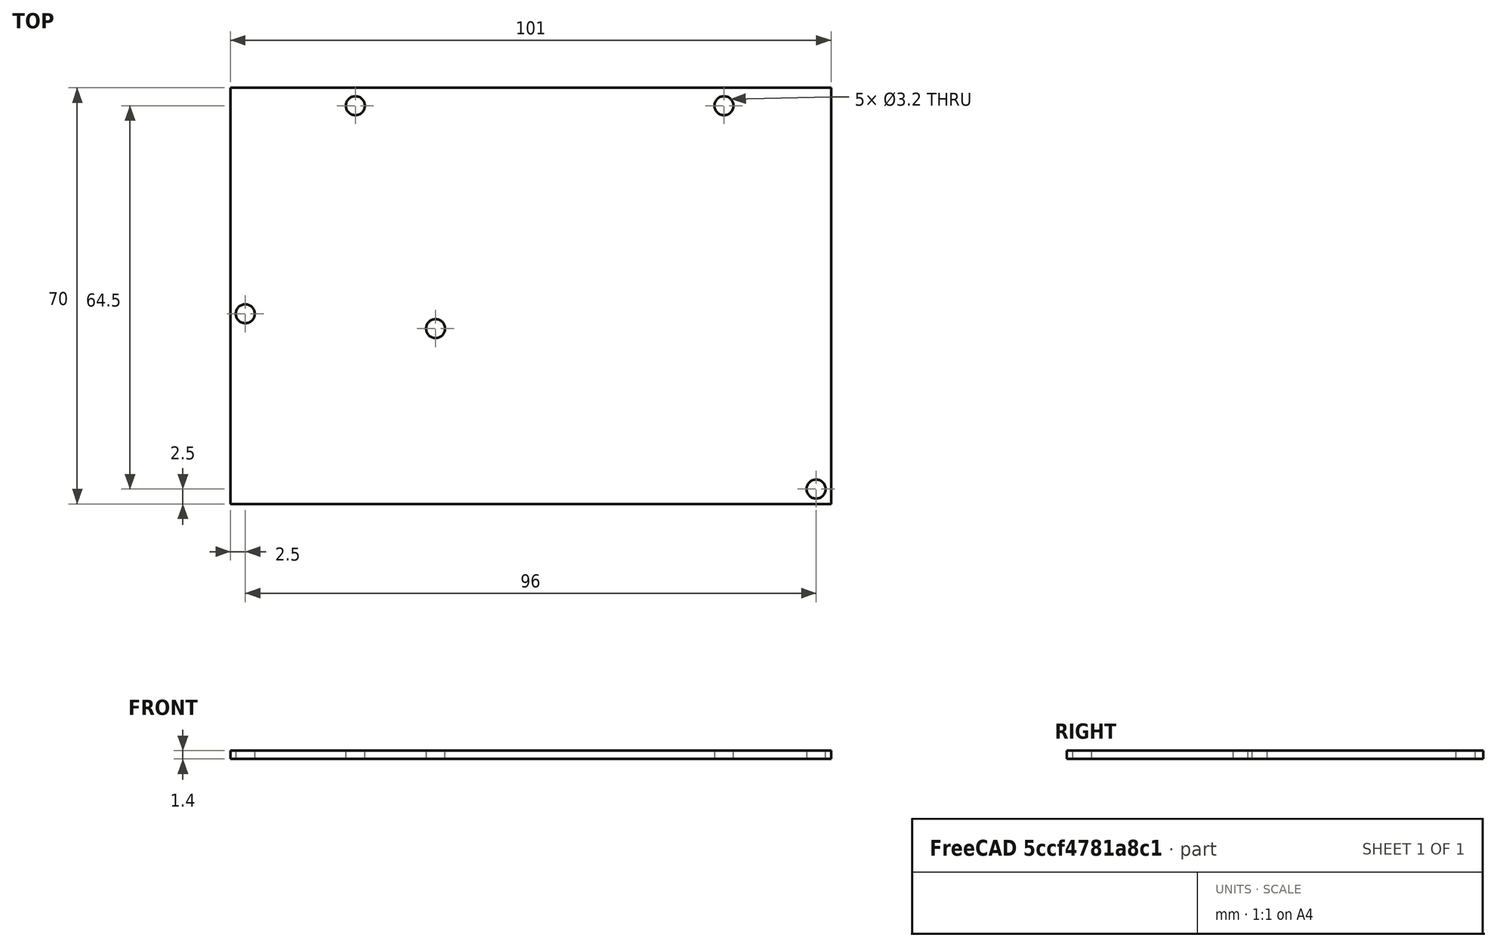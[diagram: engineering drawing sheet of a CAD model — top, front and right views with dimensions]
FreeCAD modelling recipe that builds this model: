
FCSTD DOCUMENT  (FreeCAD 1.0R39109 (Git))
Label: bigtreetech-mini-e3-v2.0
License: All rights reserved
LicenseURL: http://en.wikipedia.org/wiki/All_rights_reserved
objects: Sketcher::SketchObject×1, PartDesign::Pad×1, PartDesign::Body×1
note: 6 computed .brp shape members not serialized (recipe doc carries the construction recipe); baked Part::Feature solids carry a one-line shape summary decoded from their .brp

FEATURE [Sketcher::SketchObject] Sketch
  ArcFitTolerance = 1e-06
  AttachmentSupport = -> [XY_Plane572]
  FullyConstrained = true
  MakeInternals = false
  MapMode = 5
  sketch-geometry (9):
    g0: LineSegment StartX=-50.5 StartY=35 StartZ=0 EndX=-50.5 EndY=-35 EndZ=0
    g1: LineSegment StartX=-50.5 StartY=-35 StartZ=0 EndX=50.5 EndY=-35 EndZ=0
    g2: LineSegment StartX=50.5 StartY=-35 StartZ=0 EndX=50.5 EndY=35 EndZ=0
    g3: LineSegment StartX=50.5 StartY=35 StartZ=0 EndX=-50.5 EndY=35 EndZ=0
    g4: Circle CenterX=-48 CenterY=-3 CenterZ=0 NormalX=0 NormalY=0 NormalZ=1 AngleXU=0 Radius=1.6
    g5: Circle CenterX=-16 CenterY=-5.5 CenterZ=0 NormalX=0 NormalY=0 NormalZ=1 AngleXU=0 Radius=1.6
    g6: Circle CenterX=48 CenterY=-32.5 CenterZ=0 NormalX=0 NormalY=0 NormalZ=1 AngleXU=0 Radius=1.6
    g7: Circle CenterX=32.5 CenterY=32 CenterZ=0 NormalX=0 NormalY=0 NormalZ=1 AngleXU=0 Radius=1.6
    g8: Circle CenterX=-29.5 CenterY=32 CenterZ=0 NormalX=0 NormalY=0 NormalZ=1 AngleXU=0 Radius=1.6
  constraints (28):
    c: Coincident(g0,g1)
    c: Coincident(g1,g2)
    c: Coincident(g2,g3)
    c: Coincident(g3,g0)
    c: Vertical(g0)
    c: Vertical(g2)
    c: Horizontal(g1)
    c: Horizontal(g3)
    c: Symmetric(g1,g0,g-1)
    c: DistanceX(g3,g3) = 101
    c: DistanceY(g0,g0) = 70
    c: Equal(g8,g4)
    c: Equal(g4,g5)
    c: Equal(g5,g6)
    c: Equal(g6,g7)
    c: Diameter(g8) = 3.2
    c: DistanceY(g7,g2) = 3
    c: Horizontal(g7,g8)
    c: DistanceX(g8,g7) = 62
    c: DistanceX(g7,g2) = 18
    c: DistanceX(g0,g8) = 21
    c: DistanceY(g4,g8) = 35
    c: DistanceY(g5,g4) = 2.5
    c: DistanceX(g4,g5) = 32
    c: DistanceX(g0,g4) = 2.5
    c: DistanceX(g6,g1) = 2.5
    c: DistanceY(g1,g6) = 2.5
    c: DistanceY(g0,g4) = 32
FEATURE [PartDesign::Pad] Pad
  Direction = (0,0,1)
  Length = 1.4
  Length2 = 10
  Profile = -> Sketch
  ReferenceAxis = -> Sketch [N_Axis]
  Suppressed = false
  Type = 0
FEATURE [PartDesign::Body] Body  label="PCB-simple"
  AllowCompound = false
  Group = -> [Sketch,Pad]
  Origin = -> Origin572
  Tip = -> Pad
